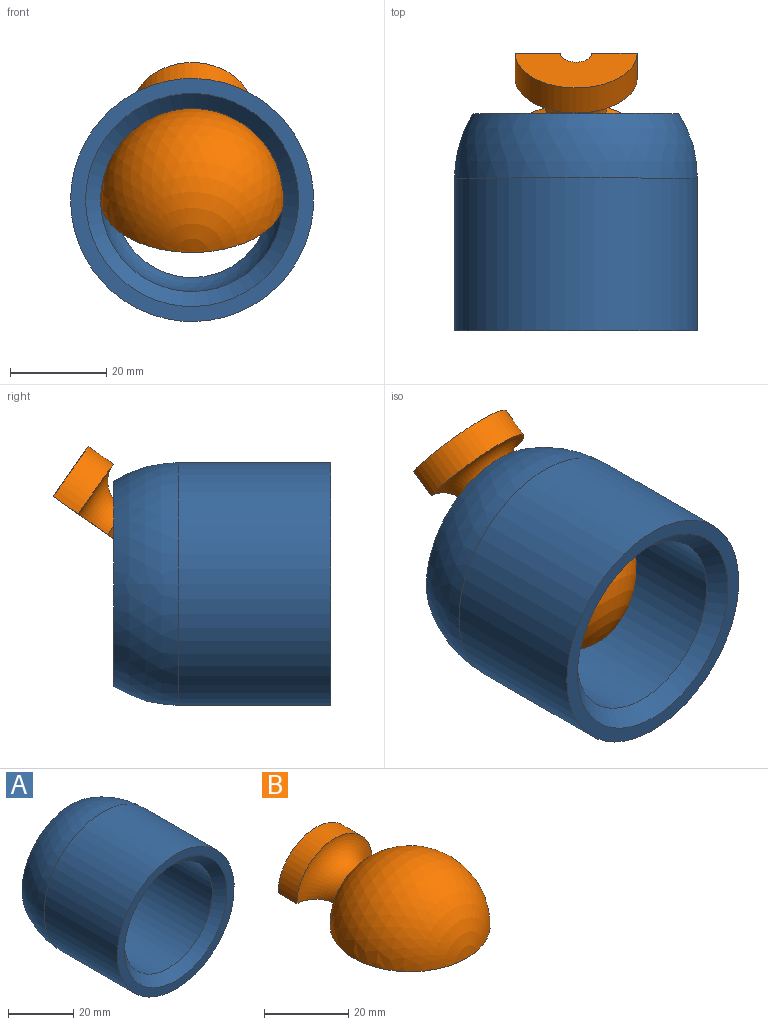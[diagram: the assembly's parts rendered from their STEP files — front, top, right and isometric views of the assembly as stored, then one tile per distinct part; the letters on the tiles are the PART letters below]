
ASSEMBLY  parts=2 mates=1
PART A: 7 faces, bbox 50.6x45.2x50.6 mm
  f0: cylinder r=19.05mm len=38.1mm, axis (0,1,0), area 3420.3mm2, adj f1,f6
  f1: cone r=19.05mm half-angle=44.5deg, axis (0,-1,0), area 577mm2, adj f0,f2
  f2: plane 50.6x50.6mm, normal (0,-1,0), area 466.1mm2, adj f1,f3
  f3: cylinder r=25.3mm len=50.6mm, axis (0,1,0), area 5047.2mm2, adj f2,f4
  f4: sphere r=25.3mm, area 2137.6mm2, adj f3,f5
  f5: cone r=16.14mm half-angle=57.9deg, axis (0,1,0), area 737.7mm2, adj f4,f6
  f6: sphere r=19.05mm, area 1211.9mm2, adj f0,f5
PART B: 9 faces, bbox 38.1x50.8x19.1 mm
  f0: plane 50.8x38.1mm, normal (0,0,-1), area 1116.1mm2, adj f1,f2,f3,f4,f5,f6,f7,f8
  f1: sphere r=19.05mm, area 2212.8mm2, adj f0,f2
  f2: torus R=12.7mm, axis (0,1,0), area 294mm2, adj f0,f1,f3
  f3: cylinder r=12.7mm len=25.4mm, axis (0,1,0), area 253.4mm2, adj f0,f2,f4
  f4: plane 25.4x12.7mm, normal (0,1,0), area 236.6mm2, adj f0,f3,f5
  f5: cylinder r=3.26mm len=31.75mm, axis (0,-1,0), area 325.6mm2, adj f0,f4,f6
  f6: plane 12.7x6.35mm, normal (0,-1,0), area 46.6mm2, adj f0,f5,f7
  f7: cylinder r=6.35mm len=12.7mm, axis (0,-1,0), area 126.7mm2, adj f0,f6,f8
  f8: plane 12.7x6.35mm, normal (0,1,0), area 63.3mm2, adj f0,f7
PLACE A t=(0.48,-11.22,-14.34)mm
PLACE B rot(axis=(1,0,0),35deg) t=(60.42,-11.22,-14.34)mm
MATE ball B.f0 <-> A.f4  axis (0,0.57,-0.82) through (60.42,-11.22,-14.34)mm
